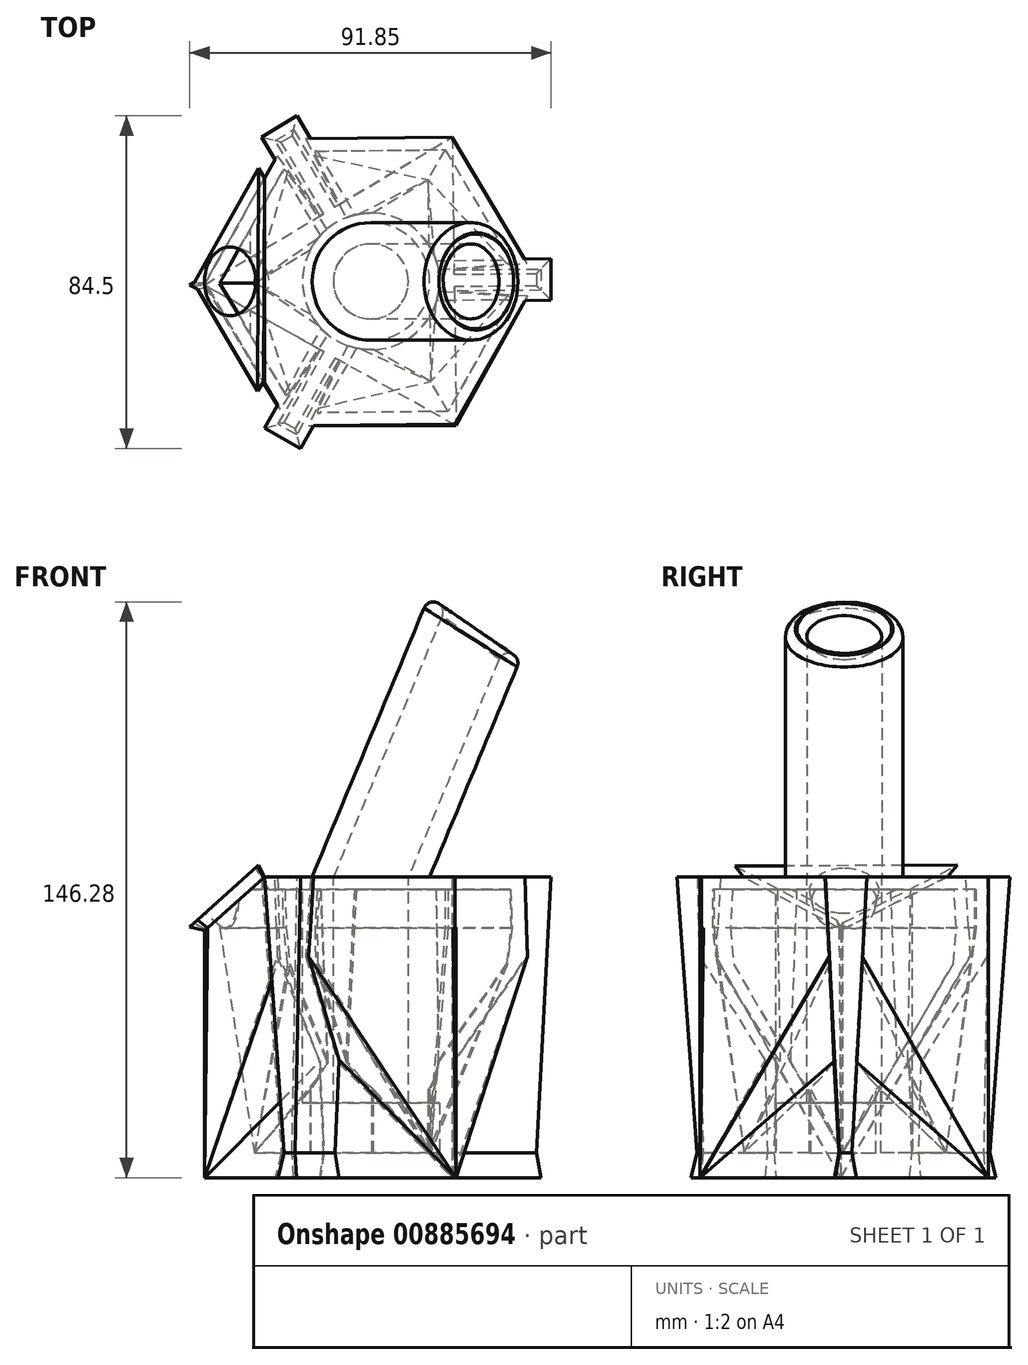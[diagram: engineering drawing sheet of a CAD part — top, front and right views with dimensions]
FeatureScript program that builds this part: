
annotation { "Feature Type Name" : "Feature", "Feature Type Description" : "" }
export const myFeature = defineFeature(function(context is Context, id is Id, definition is map)
    precondition{}
    {
        {
            var Q0;
            Q0=qCreatedBy(makeId("Top.planeOp"),FACE);
            var sketch = newSketch(context, id + "F0", { "sketchPlane" : qUnion([Q0])});
            skCircle(sketch, "E0.cCircle", {"center": v(0, -0.3) * mm, "radius": 21.17 * mm, "construction": true});
            skLineSegment(sketch, "E0.0", {"start": v(20.65, 36.66) * mm, "end": v(21.68, -36.66) * mm});
            skLineSegment(sketch, "E0.1", {"start": v(21.68, -36.66) * mm, "end": v(-42.33, -0.88) * mm});
            skLineSegment(sketch, "E0.2", {"start": v(-42.33, -0.88) * mm, "end": v(20.65, 36.66) * mm});
            skPoint(sketch, "E0.0.midPoint", {"position": v(21.16, 0) * mm});
            skSolve(sketch);
        }
        {
            var Q0;
            Q0=qCreatedBy(makeId("Top.planeOp"),FACE);
            cPlane(context, id + "F1", {"entities" : qUnion([Q0]), "cplaneType" : CPlaneType.OFFSET, "offset" : 63.5 * mm, "width" : 152.4 * mm, "height" : 152.4 * mm});
        }
        {
            var Q0;
            Q0=qCreatedBy(id+"F1.planeOp",FACE);
            var sketch = newSketch(context, id + "F2", { "sketchPlane" : qUnion([Q0])});
            skCircle(sketch, "E1.cCircle", {"center": v(0, 0) * mm, "radius": 36.44 * mm, "construction": true});
            skLineSegment(sketch, "E1.0", {"start": v(42.07, 0.44) * mm, "end": v(21.42, -36.22) * mm});
            skLineSegment(sketch, "E1.1", {"start": v(21.42, -36.22) * mm, "end": v(-20.65, -36.66) * mm});
            skLineSegment(sketch, "E1.2", {"start": v(-20.65, -36.66) * mm, "end": v(-42.07, -0.44) * mm});
            skLineSegment(sketch, "E1.3", {"start": v(-42.07, -0.44) * mm, "end": v(-21.42, 36.22) * mm});
            skLineSegment(sketch, "E1.4", {"start": v(-21.42, 36.22) * mm, "end": v(20.65, 36.66) * mm});
            skLineSegment(sketch, "E1.5", {"start": v(20.65, 36.66) * mm, "end": v(42.07, 0.44) * mm});
            skPoint(sketch, "E1.0.midPoint", {"position": v(31.75, -17.89) * mm});
            skSolve(sketch);
        }
        {
            var Q0;
            Q0=qCreatedBy(makeId("Front.planeOp"),FACE);
            var sketch = newSketch(context, id + "F3", { "sketchPlane" : qUnion([Q0])});
            skLineSegment(sketch, "E2", {"start": v(-42.33, 0) * mm, "end": v(-42.07, 63.5) * mm});
            skSolve(sketch);
        }
        {
            var Q0;
            Q0=sQuery(id+"F3.wireOp",EDGE,"E2");
            var Q1;
            Q1=sQuery(id+"F0.wireOp",VERTEX,"E0.2.start");
            var Q2;
            Q2=makeQuery(id+"F2.imprint","IMPRINT",FACE,{"disambiguationData":[TD([[makeQuery(id+"F2.imprint","IMPRINT",EDGE,{"derivedFrom":sQuery(id+"F2.wireOp",EDGE,"E1.0")}),-1.0]])]});
            var Q3;
            Q3=sQuery(id+"F3.wireOp",VERTEX,"E2.end");
            var Q4;
            Q4=sQuery(id+"F0.wireOp",VERTEX,"E0.2.start");
            loft(context, id + "F4", {"spine" : qUnion([Q0]), "sheetProfilesArray" : [{ "sheetProfileEntities" : qUnion([Q1]) }, { "sheetProfileEntities" : qUnion([Q2]) }], "connections" : [{ "connectionEntities" : qUnion([Q3, Q4]), "connectionEdgeQueries" : qUnion([]), "connectionEdgeParameters" : [] }]});
        }
        {
            var Q1;
            Q1=makeQuery(id+"F2.imprint","IMPRINT",FACE,{"disambiguationData":[TD([[makeQuery(id+"F2.imprint","IMPRINT",EDGE,{"derivedFrom":sQuery(id+"F2.wireOp",EDGE,"E1.0")}),-1.0]])]});
            var Q2;
            Q2=sQuery(id+"F0.wireOp",VERTEX,"E0.0.end");
            loft(context, id + "F5", {"operationType" : NewBodyOperationType.ADD, "sheetProfilesArray" : [{ "sheetProfileEntities" : qUnion([Q1]) }, { "sheetProfileEntities" : qUnion([Q2]) }]});
        }
        {
            var Q1;
            Q1=makeQuery(id+"F2.imprint","IMPRINT",FACE,{"disambiguationData":[TD([[makeQuery(id+"F2.imprint","IMPRINT",EDGE,{"derivedFrom":sQuery(id+"F2.wireOp",EDGE,"E1.0")}),-1.0]])]});
            var Q2;
            Q2=sQuery(id+"F0.wireOp",VERTEX,"E0.0.start");
            loft(context, id + "F6", {"operationType" : NewBodyOperationType.ADD, "sheetProfilesArray" : [{ "sheetProfileEntities" : qUnion([Q1]) }, { "sheetProfileEntities" : qUnion([Q2]) }]});
        }
        {
            var Q0;
            Q0=makeQuery(id+"F0.imprint","IMPRINT",FACE,{"disambiguationData":[TD([[makeQuery(id+"F0.imprint","IMPRINT",EDGE,{"derivedFrom":sQuery(id+"F0.wireOp",EDGE,"E0.0")}),-1.0]])]});
            var Q1;
            Q1=makeQuery(id+"F4.opLoft","CAP_FACE",FACE,{"disambiguationData":[OSD([makeQuery(id+"F2.imprint","IMPRINT",FACE,{"disambiguationData":[TD([[makeQuery(id+"F2.imprint","IMPRINT",EDGE,{"derivedFrom":sQuery(id+"F2.wireOp",EDGE,"E1.0")}),-1.0]])]})])],"isStart":true});
            extrude(context, id + "F7", {"entities" : qUnion([Q0]), "operationType" : NewBodyOperationType.ADD, "endBound" : BoundingType.UP_TO_SURFACE, "depth" : 66.55 * mm, "endBoundEntityFace" : qUnion([Q1]), "offsetDistance" : 25.4 * mm});
        }
        {
            var Q0;
            Q0=makeQuery(id+"F2.imprint","IMPRINT",FACE,{"disambiguationData":[TD([[makeQuery(id+"F2.imprint","IMPRINT",EDGE,{"derivedFrom":sQuery(id+"F2.wireOp",EDGE,"E1.0")}),-1.0]])]});
            extrude(context, id + "F8", {"entities" : qUnion([Q0]), "operationType" : NewBodyOperationType.ADD, "depth" : 7.87 * mm, "offsetDistance" : 25.4 * mm});
        }
        {
            var Q0;
            Q0=qCreatedBy(id+"F1.planeOp",FACE);
            var sketch = newSketch(context, id + "F9", { "sketchPlane" : qUnion([Q0])});
            skCircle(sketch, "E3.cCircle", {"center": v(0, 0) * mm, "radius": 38.41 * mm, "construction": true});
            skLineSegment(sketch, "E3.0", {"start": v(18.85, 33.46) * mm, "end": v(38.4, 0.4) * mm});
            skLineSegment(sketch, "E3.1", {"start": v(38.4, 0.4) * mm, "end": v(19.55, -33.06) * mm});
            skLineSegment(sketch, "E3.2", {"start": v(19.55, -33.06) * mm, "end": v(-18.85, -33.46) * mm});
            skLineSegment(sketch, "E3.3", {"start": v(-18.85, -33.46) * mm, "end": v(-38.4, -0.4) * mm});
            skLineSegment(sketch, "E3.4", {"start": v(-38.4, -0.4) * mm, "end": v(-19.55, 33.06) * mm});
            skLineSegment(sketch, "E3.5", {"start": v(-19.55, 33.06) * mm, "end": v(18.85, 33.46) * mm});
            skSolve(sketch);
        }
        {
            var Q0;
            Q0 = qSketchRegion(id + "F9", true);
            var Q1;
            Q1=sQuery(id+"F9.wireOp",EDGE,"54bb823f-575e-4e5f-845b-b7277e6f640d.0");
            var Q2;
            Q2=sQuery(id+"F9.wireOp",EDGE,"54bb823f-575e-4e5f-845b-b7277e6f640d.1");
            var Q3;
            Q3=sQuery(id+"F9.wireOp",EDGE,"54bb823f-575e-4e5f-845b-b7277e6f640d.2");
            extrude(context, id + "F10", {"entities" : qUnion([Q0]), "operationType" : NewBodyOperationType.REMOVE, "surfaceEntities" : qUnion([Q1, Q2, Q3]), "depth" : 36.83 * mm, "offsetDistance" : 25.4 * mm});
        }
        {
            var Q0;
            Q0=qCreatedBy(id+"F1.planeOp",FACE);
            var sketch = newSketch(context, id + "F11", { "sketchPlane" : qUnion([Q0])});
            skCircle(sketch, "E4.cCircle", {"center": v(0, 0) * mm, "radius": 38.41 * mm, "construction": true});
            skLineSegment(sketch, "E4.0", {"start": v(18.85, 33.46) * mm, "end": v(38.4, 0.4) * mm});
            skLineSegment(sketch, "E4.1", {"start": v(38.4, 0.4) * mm, "end": v(19.55, -33.06) * mm});
            skLineSegment(sketch, "E4.2", {"start": v(19.55, -33.06) * mm, "end": v(-18.85, -33.46) * mm});
            skLineSegment(sketch, "E4.3", {"start": v(-18.85, -33.46) * mm, "end": v(-38.4, -0.4) * mm});
            skLineSegment(sketch, "E4.4", {"start": v(-38.4, -0.4) * mm, "end": v(-19.55, 33.06) * mm});
            skLineSegment(sketch, "E4.5", {"start": v(-19.55, 33.06) * mm, "end": v(18.85, 33.46) * mm});
            skSolve(sketch);
        }
        {
            var Q0;
            Q0=qCreatedBy(makeId("Top.planeOp"),FACE);
            cPlane(context, id + "F12", {"entities" : qUnion([Q0]), "cplaneType" : CPlaneType.OFFSET, "offset" : 6.35 * mm, "width" : 152.4 * mm, "height" : 152.4 * mm});
        }
        {
            var Q0;
            Q0=qCreatedBy(id+"F12.planeOp",FACE);
            var sketch = newSketch(context, id + "F13", { "sketchPlane" : qUnion([Q0])});
            skCircle(sketch, "E5.cCircle", {"center": v(0, 0) * mm, "radius": 29.63 * mm, "construction": true});
            skLineSegment(sketch, "E5.0", {"start": v(14.45, 25.86) * mm, "end": v(15.17, -25.45) * mm});
            skLineSegment(sketch, "E5.1", {"start": v(15.17, -25.45) * mm, "end": v(-29.62, -0.41) * mm});
            skLineSegment(sketch, "E5.2", {"start": v(-29.62, -0.41) * mm, "end": v(14.45, 25.86) * mm});
            skSolve(sketch);
        }
        {
            var Q1;
            Q1=makeQuery(id+"F11.imprint","IMPRINT",FACE,{"disambiguationData":[TD([[makeQuery(id+"F11.imprint","IMPRINT",EDGE,{"derivedFrom":sQuery(id+"F11.wireOp",EDGE,"E4.0")}),-1.0]])]});
            var Q2;
            Q2=sQuery(id+"F13.wireOp",VERTEX,"E5.1.end");
            loft(context, id + "F14", {"operationType" : NewBodyOperationType.REMOVE, "sheetProfilesArray" : [{ "sheetProfileEntities" : qUnion([Q1]) }, { "sheetProfileEntities" : qUnion([Q2]) }]});
        }
        {
            var Q1;
            Q1=makeQuery(id+"F11.imprint","IMPRINT",FACE,{"disambiguationData":[TD([[makeQuery(id+"F11.imprint","IMPRINT",EDGE,{"derivedFrom":sQuery(id+"F11.wireOp",EDGE,"E4.0")}),-1.0]])]});
            var Q2;
            Q2=sQuery(id+"F13.wireOp",VERTEX,"E5.0.start");
            loft(context, id + "F15", {"operationType" : NewBodyOperationType.REMOVE, "sheetProfilesArray" : [{ "sheetProfileEntities" : qUnion([Q1]) }, { "sheetProfileEntities" : qUnion([Q2]) }]});
        }
        {
            var Q1;
            Q1=makeQuery(id+"F11.imprint","IMPRINT",FACE,{"disambiguationData":[TD([[makeQuery(id+"F11.imprint","IMPRINT",EDGE,{"derivedFrom":sQuery(id+"F11.wireOp",EDGE,"E4.0")}),-1.0]])]});
            var Q2;
            Q2=sQuery(id+"F13.wireOp",VERTEX,"E5.0.end");
            loft(context, id + "F16", {"operationType" : NewBodyOperationType.REMOVE, "sheetProfilesArray" : [{ "sheetProfileEntities" : qUnion([Q1]) }, { "sheetProfileEntities" : qUnion([Q2]) }]});
        }
        {
            var Q0;
            Q0 = qSketchRegion(id + "F13", true);
            extrude(context, id + "F17", {"entities" : qUnion([Q0]), "operationType" : NewBodyOperationType.REMOVE, "depth" : 76.2 * mm, "offsetDistance" : 25.4 * mm});
        }
        {
            var Q0;
            Q0=makeQuery(id+"F8.opExtrude","CAP_FACE",FACE,{"disambiguationData":[OSD([sQuery(id+"F2.wireOp",EDGE,"E1.0"),sQuery(id+"F2.wireOp",EDGE,"E1.1"),sQuery(id+"F2.wireOp",EDGE,"E1.2"),sQuery(id+"F2.wireOp",EDGE,"E1.3"),sQuery(id+"F2.wireOp",EDGE,"E1.4"),sQuery(id+"F2.wireOp",EDGE,"E1.5")])],"isStart":false});
            extrude(context, id + "F18", {"entities" : qUnion([Q0]), "operationType" : NewBodyOperationType.ADD, "depth" : 5.08 * mm, "offsetDistance" : 25.4 * mm});
        }
        {
            var Q0;
            Q0=qCreatedBy(id+"F12.planeOp",FACE);
            var sketch = newSketch(context, id + "F19", { "sketchPlane" : qUnion([Q0])});
            skLineSegment(sketch, "E6", {"start": v(-20.05, 37.02) * mm, "end": v(-22.79, 35.4) * mm});
            skLineSegment(sketch, "E7", {"start": v(-22.79, 35.4) * mm, "end": v(-1.83, 0) * mm});
            skLineSegment(sketch, "E8", {"start": v(-20.05, 37.02) * mm, "end": v(0.92, 1.59) * mm});
            skLineSegment(sketch, "E9", {"start": v(-1.83, 0) * mm, "end": v(-22.04, -35.88) * mm});
            skLineSegment(sketch, "E10", {"start": v(-22.04, -35.88) * mm, "end": v(-19.27, -37.44) * mm});
            skLineSegment(sketch, "E11", {"start": v(-19.27, -37.44) * mm, "end": v(0.92, -1.59) * mm});
            skLineSegment(sketch, "E12", {"start": v(0.92, -1.59) * mm, "end": v(42.1, -1.15) * mm});
            skLineSegment(sketch, "E13", {"start": v(42.1, -1.15) * mm, "end": v(42.06, 2.03) * mm});
            skLineSegment(sketch, "E14", {"start": v(42.06, 2.03) * mm, "end": v(0.92, 1.59) * mm});
            skSolve(sketch);
        }
        {
            var Q0;
            Q0 = qSketchRegion(id + "F19", true);
            var Q1;
            Q1=makeQuery(id+"F18.opExtrude","CAP_FACE",FACE,{"disambiguationData":[OSD([sQuery(id+"F2.wireOp",EDGE,"E1.0"),sQuery(id+"F2.wireOp",EDGE,"E1.1"),sQuery(id+"F2.wireOp",EDGE,"E1.2"),sQuery(id+"F2.wireOp",EDGE,"E1.3"),sQuery(id+"F2.wireOp",EDGE,"E1.4"),sQuery(id+"F2.wireOp",EDGE,"E1.5")])],"isStart":false});
            var Q2;
            Q2=makeQuery(id+"F7.opExtrude","CAP_FACE",FACE,{"disambiguationData":[OSD([sQuery(id+"F0.wireOp",EDGE,"E0.0"),sQuery(id+"F0.wireOp",EDGE,"E0.1"),sQuery(id+"F0.wireOp",EDGE,"E0.2")])],"isStart":true});
            extrude(context, id + "F20", {"entities" : qUnion([Q0]), "operationType" : NewBodyOperationType.ADD, "endBound" : BoundingType.UP_TO_SURFACE, "depth" : 25.4 * mm, "endBoundEntityFace" : qUnion([Q1]), "offsetDistance" : 25.4 * mm, "hasDraft" : true, "draftAngle" : 3 * degree, "hasSecondDirection" : true, "secondDirectionBound" : SecondDirectionBoundingType.UP_TO_SURFACE, "secondDirectionOppositeDirection" : true, "secondDirectionDepth" : 25.4 * mm, "secondDirectionBoundEntityFace" : qUnion([Q2]), "hasSecondDirectionDraft" : true, "secondDirectionDraftAngle" : 10 * degree});
        }
        {
            var Q0;
            Q0=makeQuery(id+"F20.boolean.opBoolean","MERGE",FACE,{"derivedFrom":[makeQuery(id+"F18.opExtrude","CAP_FACE",FACE,{"disambiguationData":[OSD([sQuery(id+"F2.wireOp",EDGE,"E1.0"),sQuery(id+"F2.wireOp",EDGE,"E1.1"),sQuery(id+"F2.wireOp",EDGE,"E1.2"),sQuery(id+"F2.wireOp",EDGE,"E1.3"),sQuery(id+"F2.wireOp",EDGE,"E1.4"),sQuery(id+"F2.wireOp",EDGE,"E1.5")])],"isStart":false}),makeQuery(id+"F20.opExtrude","CAP_FACE",FACE,{"disambiguationData":[OSD([sQuery(id+"F19.wireOp",EDGE,"E6"),sQuery(id+"F19.wireOp",EDGE,"E7"),sQuery(id+"F19.wireOp",EDGE,"E8"),sQuery(id+"F19.wireOp",EDGE,"E9"),sQuery(id+"F19.wireOp",EDGE,"E10"),sQuery(id+"F19.wireOp",EDGE,"E11"),sQuery(id+"F19.wireOp",EDGE,"E12"),sQuery(id+"F19.wireOp",EDGE,"E13"),sQuery(id+"F19.wireOp",EDGE,"E14")])],"isStart":false})]});
            var sketch = newSketch(context, id + "F21", { "sketchPlane" : qUnion([Q0])});
            skCircle(sketch, "E15", {"center": v(0, 0) * mm, "radius": 9.53 * mm});
            skCircle(sketch, "E16", {"center": v(0, 0) * mm, "radius": 17.37 * mm});
            skSolve(sketch);
        }
        {
            var Q0;
            Q0 = qSketchRegion(id + "F21", true);
            var Q1;
            Q1=makeQuery(id+"F20.boolean.opBoolean","MERGE",FACE,{"derivedFrom":[makeQuery(id+"F7.opExtrude","CAP_FACE",FACE,{"disambiguationData":[OSD([sQuery(id+"F0.wireOp",EDGE,"E0.0"),sQuery(id+"F0.wireOp",EDGE,"E0.1"),sQuery(id+"F0.wireOp",EDGE,"E0.2")])],"isStart":true}),makeQuery(id+"F20.opExtrude","CAP_FACE",FACE,{"disambiguationData":[OSD([sQuery(id+"F19.wireOp",EDGE,"E6"),sQuery(id+"F19.wireOp",EDGE,"E7"),sQuery(id+"F19.wireOp",EDGE,"E8"),sQuery(id+"F19.wireOp",EDGE,"E9"),sQuery(id+"F19.wireOp",EDGE,"E10"),sQuery(id+"F19.wireOp",EDGE,"E11"),sQuery(id+"F19.wireOp",EDGE,"E12"),sQuery(id+"F19.wireOp",EDGE,"E13"),sQuery(id+"F19.wireOp",EDGE,"E14")])],"isStart":true})]});
            extrude(context, id + "F22", {"entities" : qUnion([Q0]), "operationType" : NewBodyOperationType.ADD, "endBound" : BoundingType.UP_TO_SURFACE, "oppositeDirection" : true, "depth" : 70.61 * mm, "endBoundEntityFace" : qUnion([Q1]), "offsetDistance" : 25.4 * mm});
        }
        {
            var Q0;
            {var subQ0=sQuery(id+"F21.wireOp",EDGE,"E15");var subQ12=sQuery(id+"F19.wireOp",EDGE,"E8");var subQ37=sQuery(id+"F9.wireOp",EDGE,"E3.5");var subQ38=makeQuery(id+"F20.boolean.opBoolean","SPLIT",EDGE,{"disambiguationData":[TD([makeQuery(id+"F10.boolean.opBoolean","COPY",FACE,{"derivedFrom":makeQuery(id+"F10.opExtrude","SWEPT_FACE",FACE,{"disambiguationData":[OSD([subQ37])]})})])],"derivedFrom":makeQuery(id+"F20.opExtrude","CAP_EDGE",EDGE,{"disambiguationData":[OSD([subQ12])],"isStart":false})});var subQ40=makeQuery(id+"F21.imprint","INTERSECT",VERTEX,{"derivedFrom":[subQ38,subQ0]});Q0=makeQuery(id+"F21.imprint","IMPRINT",FACE,{"disambiguationData":[TD([[makeQuery(id+"F21.imprint","IMPRINT",EDGE,{"disambiguationData":[TD([[subQ40,-1.0]])],"derivedFrom":subQ0}),1.0]])]});}
            var Q1;
            Q1=makeQuery(id+"F20.*.split.splitOp","SPLIT",FACE,{"derivedFrom":makeQuery(id+"F20.opExtrude","SWEPT_FACE",FACE,{"disambiguationData":[OSD([sQuery(id+"F19.wireOp",EDGE,"E14")])]}),"isFromBackBody":true});
            extrude(context, id + "F23", {"entities" : qUnion([Q0]), "operationType" : NewBodyOperationType.REMOVE, "oppositeDirection" : true, "depth" : 69.85 * mm, "endBoundEntityFace" : qUnion([Q1]), "offsetDistance" : 25.4 * mm});
        }
        {
            var Q0;
            Q0=qCreatedBy(id+"F12.planeOp",FACE);
            var sketch = newSketch(context, id + "F24", { "sketchPlane" : qUnion([Q0])});
            skCircle(sketch, "E17", {"center": v(0, 0) * mm, "radius": 17.37 * mm});
            skSolve(sketch);
        }
        {
            var Q0;
            Q0 = qSketchRegion(id + "F24", true);
            extrude(context, id + "F25", {"entities" : qUnion([Q0]), "operationType" : NewBodyOperationType.REMOVE, "depth" : 12.7 * mm, "offsetDistance" : 25.4 * mm});
        }
        {
            var Q0;
            {var subQ8=sQuery(id+"F19.wireOp",EDGE,"E6");Q0=makeQuery(id+"F21.imprint","IMPRINT",FACE,{"disambiguationData":[TD([[makeQuery(id+"F21.imprint","IMPRINT",EDGE,{"derivedFrom":makeQuery(id+"F20.opExtrude","CAP_EDGE",EDGE,{"disambiguationData":[OSD([subQ8])],"isStart":false})}),1.0]])]});}
            var sketch = newSketch(context, id + "F26", { "sketchPlane" : qUnion([Q0])});
            skCircle(sketch, "E18.cCircle", {"center": v(0, 0) * mm, "radius": 42.08 * mm, "construction": true});
            skLineSegment(sketch, "E18.0", {"start": v(20.65, 36.66) * mm, "end": v(42.07, 0.44) * mm});
            skLineSegment(sketch, "E18.1", {"start": v(42.07, 0.44) * mm, "end": v(21.42, -36.22) * mm});
            skLineSegment(sketch, "E18.2", {"start": v(21.42, -36.22) * mm, "end": v(-20.65, -36.66) * mm});
            skLineSegment(sketch, "E18.3", {"start": v(-20.65, -36.66) * mm, "end": v(-42.07, -0.44) * mm});
            skLineSegment(sketch, "E18.4", {"start": v(-42.07, -0.44) * mm, "end": v(-21.42, 36.22) * mm});
            skLineSegment(sketch, "E18.5", {"start": v(-21.42, 36.22) * mm, "end": v(20.65, 36.66) * mm});
            skSolve(sketch);
        }
        {
            var Q0;
            Q0 = qSketchRegion(id + "F26", true);
            extrude(context, id + "F27", {"entities" : qUnion([Q0]), "operationType" : NewBodyOperationType.ADD, "oppositeDirection" : true, "depth" : 3.17 * mm, "offsetDistance" : 25.4 * mm});
        }
        {
            var Q0;
            {var subQ0=sQuery(id+"F21.wireOp",EDGE,"E15");var subQ8=sQuery(id+"F9.wireOp",EDGE,"E3.4");var subQ11=sQuery(id+"F19.wireOp",EDGE,"E7");var subQ14=makeQuery(id+"F20.boolean.opBoolean","SPLIT",EDGE,{"disambiguationData":[TD([makeQuery(id+"F10.boolean.opBoolean","COPY",FACE,{"derivedFrom":makeQuery(id+"F10.opExtrude","SWEPT_FACE",FACE,{"disambiguationData":[OSD([subQ8])]})})])],"derivedFrom":makeQuery(id+"F20.opExtrude","CAP_EDGE",EDGE,{"disambiguationData":[OSD([subQ11])],"isStart":false})});var subQ15=makeQuery(id+"F21.imprint","INTERSECT",VERTEX,{"derivedFrom":[subQ14,subQ0]});Q0=makeQuery(id+"F21.imprint","IMPRINT",FACE,{"disambiguationData":[TD([[makeQuery(id+"F21.imprint","IMPRINT",EDGE,{"disambiguationData":[TD([[subQ15,-1.0]])],"derivedFrom":subQ0}),1.0]])]});}
            var Q1;
            {var subQ0=sQuery(id+"F21.wireOp",EDGE,"E15");var subQ12=sQuery(id+"F19.wireOp",EDGE,"E8");var subQ37=sQuery(id+"F9.wireOp",EDGE,"E3.5");var subQ38=makeQuery(id+"F20.boolean.opBoolean","SPLIT",EDGE,{"disambiguationData":[TD([makeQuery(id+"F10.boolean.opBoolean","COPY",FACE,{"derivedFrom":makeQuery(id+"F10.opExtrude","SWEPT_FACE",FACE,{"disambiguationData":[OSD([subQ37])]})})])],"derivedFrom":makeQuery(id+"F20.opExtrude","CAP_EDGE",EDGE,{"disambiguationData":[OSD([subQ12])],"isStart":false})});var subQ40=makeQuery(id+"F21.imprint","INTERSECT",VERTEX,{"derivedFrom":[subQ38,subQ0]});Q1=makeQuery(id+"F21.imprint","IMPRINT",FACE,{"disambiguationData":[TD([[makeQuery(id+"F21.imprint","IMPRINT",EDGE,{"disambiguationData":[TD([[subQ40,-1.0]])],"derivedFrom":subQ0}),1.0]])]});}
            var Q2;
            {var subQ0=sQuery(id+"F21.wireOp",EDGE,"E15");var subQ2=sQuery(id+"F19.wireOp",EDGE,"E11");var subQ11=sQuery(id+"F9.wireOp",EDGE,"E3.2");var subQ14=makeQuery(id+"F20.boolean.opBoolean","SPLIT",EDGE,{"disambiguationData":[TD([makeQuery(id+"F10.boolean.opBoolean","COPY",FACE,{"derivedFrom":makeQuery(id+"F10.opExtrude","SWEPT_FACE",FACE,{"disambiguationData":[OSD([subQ11])]})})])],"derivedFrom":makeQuery(id+"F20.opExtrude","CAP_EDGE",EDGE,{"disambiguationData":[OSD([subQ2])],"isStart":false})});var subQ15=makeQuery(id+"F21.imprint","INTERSECT",VERTEX,{"derivedFrom":[subQ14,subQ0]});Q2=makeQuery(id+"F21.imprint","IMPRINT",FACE,{"disambiguationData":[TD([[makeQuery(id+"F21.imprint","IMPRINT",EDGE,{"disambiguationData":[TD([[subQ15,-1.0]])],"derivedFrom":subQ0}),1.0]])]});}
            var Q3;
            {var subQ0=sQuery(id+"F21.wireOp",EDGE,"E15");var subQ9=sQuery(id+"F19.wireOp",EDGE,"E8");var subQ11=sQuery(id+"F9.wireOp",EDGE,"E3.5");var subQ14=makeQuery(id+"F20.boolean.opBoolean","SPLIT",EDGE,{"disambiguationData":[TD([makeQuery(id+"F10.boolean.opBoolean","COPY",FACE,{"derivedFrom":makeQuery(id+"F10.opExtrude","SWEPT_FACE",FACE,{"disambiguationData":[OSD([subQ11])]})})])],"derivedFrom":makeQuery(id+"F20.opExtrude","CAP_EDGE",EDGE,{"disambiguationData":[OSD([subQ9])],"isStart":false})});var subQ15=makeQuery(id+"F21.imprint","INTERSECT",VERTEX,{"derivedFrom":[subQ14,subQ0]});Q3=makeQuery(id+"F21.imprint","IMPRINT",FACE,{"disambiguationData":[TD([[makeQuery(id+"F21.imprint","IMPRINT",EDGE,{"disambiguationData":[TD([[subQ15,1.0]])],"derivedFrom":subQ0}),1.0]])]});}
            var Q4;
            Q4=sQuery(id+"F21.wireOp",EDGE,"E15");
            extrude(context, id + "F28", {"entities" : qUnion([Q0, Q1, Q2, Q3]), "operationType" : NewBodyOperationType.REMOVE, "surfaceEntities" : qUnion([Q4]), "oppositeDirection" : true, "depth" : 6.35 * mm, "offsetDistance" : 25.4 * mm});
        }
        {
            var Q0;
            {var subQ8=sQuery(id+"F19.wireOp",EDGE,"E6");Q0=makeQuery(id+"F21.imprint","IMPRINT",FACE,{"disambiguationData":[TD([[makeQuery(id+"F21.imprint","IMPRINT",EDGE,{"derivedFrom":makeQuery(id+"F20.opExtrude","CAP_EDGE",EDGE,{"disambiguationData":[OSD([subQ8])],"isStart":false})}),1.0]])]});}
            var sketch = newSketch(context, id + "F29", { "sketchPlane" : qUnion([Q0])});
            skCircle(sketch, "E19", {"center": v(0, 0) * mm, "radius": 9.53 * mm});
            skCircle(sketch, "E20", {"center": v(0, 0) * mm, "radius": 12.7 * mm});
            skSolve(sketch);
        }
        {
            var Q0;
            {var subQ8=sQuery(id+"F19.wireOp",EDGE,"E6");Q0=makeQuery(id+"F29.imprint","IMPRINT",FACE,{"disambiguationData":[TD([[makeQuery(id+"F29.imprint","IMPRINT",EDGE,{"derivedFrom":makeQuery(id+"F21.imprint","IMPRINT",EDGE,{"derivedFrom":makeQuery(id+"F20.opExtrude","CAP_EDGE",EDGE,{"disambiguationData":[OSD([subQ8])],"isStart":false})})}),1.0]])]});}
            cPlane(context, id + "F30", {"entities" : qUnion([Q0]), "cplaneType" : CPlaneType.OFFSET, "offset" : 76.2 * mm, "width" : 152.4 * mm, "height" : 152.4 * mm});
        }
        {
            var Q0;
            Q0=qCreatedBy(id+"F30.planeOp",FACE);
            var sketch = newSketch(context, id + "F31", { "sketchPlane" : qUnion([Q0])});
            skCircle(sketch, "E21", {"center": v(31.75, 0) * mm, "radius": 9.53 * mm});
            skCircle(sketch, "E22", {"center": v(31.75, 0) * mm, "radius": 14.93 * mm});
            skSolve(sketch);
        }
        {
            var Q0;
            Q0=qCreatedBy(makeId("Front.planeOp"),FACE);
            var sketch = newSketch(context, id + "F32", { "sketchPlane" : qUnion([Q0])});
            skLineSegment(sketch, "E23", {"start": v(31.75, 152.65) * mm, "end": v(0, 76.45) * mm});
            skSolve(sketch);
        }
        {
            var Q0;
            Q0=makeQuery(id+"F29.imprint","IMPRINT",FACE,{"disambiguationData":[TD([[makeQuery(id+"F29.imprint","IMPRINT",EDGE,{"derivedFrom":sQuery(id+"F29.wireOp",EDGE,"E19")}),-1.0]])]});
            var Q1;
            Q1=makeQuery(id+"F31.imprint","IMPRINT",FACE,{"disambiguationData":[TD([[makeQuery(id+"F31.imprint","IMPRINT",EDGE,{"derivedFrom":sQuery(id+"F31.wireOp",EDGE,"E21")}),-1.0]])]});
            var Q2;
            Q2=sQuery(id+"F32.wireOp",EDGE,"E23");
            sweep(context, id + "F33", {"operationType" : NewBodyOperationType.ADD, "profiles" : qUnion([Q0, Q1]), "path" : qUnion([Q2])});
        }
        {
            var Q0;
            Q0=qCreatedBy(makeId("Front.planeOp"),FACE);
            var sketch = newSketch(context, id + "F34", { "sketchPlane" : qUnion([Q0])});
            skLineSegment(sketch, "E24", {"start": v(0, 157.7) * mm, "end": v(46.75, 125.63) * mm});
            skLineSegment(sketch, "E25", {"start": v(46.75, 125.63) * mm, "end": v(69.79, 143.24) * mm});
            skLineSegment(sketch, "E26", {"start": v(69.79, 143.24) * mm, "end": v(9.97, 177.78) * mm});
            skLineSegment(sketch, "E27", {"start": v(9.97, 177.78) * mm, "end": v(0, 157.7) * mm});
            skSolve(sketch);
        }
        {
            var Q0;
            Q0=makeQuery(id+"F34.imprint","IMPRINT",FACE,{"disambiguationData":[TD([[makeQuery(id+"F34.imprint","IMPRINT",EDGE,{"derivedFrom":sQuery(id+"F34.wireOp",EDGE,"E24")}),1.0]])]});
            var Q1;
            Q1 = qConstructionFilter(qBodyType(qCreatedBy(id + "F34" ,EDGE), BodyType.WIRE), ConstructionObject.NO);
            extrude(context, id + "F35", {"entities" : qUnion([Q0]), "operationType" : NewBodyOperationType.REMOVE, "surfaceEntities" : qUnion([Q1]), "endBound" : BoundingType.THROUGH_ALL, "oppositeDirection" : true, "depth" : 25.4 * mm, "offsetDistance" : 25.4 * mm, "hasSecondDirection" : true, "secondDirectionOppositeDirection" : false, "secondDirectionDepth" : 25.4 * mm});
        }
        {
            var Q0;
            Q0=makeQuery(id+"F35.boolean.opBoolean","INTERSECT",EDGE,{"derivedFrom":[makeQuery(id+"F33.opSweep","SWEPT_FACE",FACE,{"disambiguationData":[OSD([sQuery(id+"F29.wireOp",EDGE,"E19"),sQuery(id+"F32.wireOp",EDGE,"E23")])]}),makeQuery(id+"F35.opExtrude","SWEPT_FACE",FACE,{"disambiguationData":[OSD([sQuery(id+"F34.wireOp",EDGE,"E24")])]})]});
            var Q1;
            Q1=makeQuery(id+"F35.boolean.opBoolean","INTERSECT",EDGE,{"derivedFrom":[makeQuery(id+"F33.opSweep","SWEPT_FACE",FACE,{"disambiguationData":[OSD([sQuery(id+"F31.wireOp",EDGE,"E22"),sQuery(id+"F32.wireOp",EDGE,"E23")])]}),makeQuery(id+"F35.opExtrude","SWEPT_FACE",FACE,{"disambiguationData":[OSD([sQuery(id+"F34.wireOp",EDGE,"E24")])]})]});
            fillet(context, id + "F36", {"entities" : qUnion([Q0, Q1]), "radius" : 2.54 * mm, "tangentPropagation" : true, "allowEdgeOverflow" : false});
        }
        {
            var Q0;
            Q0=qCreatedBy(makeId("Front.planeOp"),FACE);
            var sketch = newSketch(context, id + "F37", { "sketchPlane" : qUnion([Q0])});
            skLineSegment(sketch, "E28", {"start": v(-48.75, 57.08) * mm, "end": v(-27.04, 76.45) * mm});
            skLineSegment(sketch, "E29", {"start": v(-27.04, 76.45) * mm, "end": v(-44.91, 87.8) * mm});
            skLineSegment(sketch, "E30", {"start": v(-44.91, 87.8) * mm, "end": v(-55.53, 62.05) * mm});
            skLineSegment(sketch, "E31", {"start": v(-55.53, 62.05) * mm, "end": v(-48.75, 57.08) * mm});
            skSolve(sketch);
        }
        {
            var Q0;
            Q0 = qSketchRegion(id + "F37", true);
            extrude(context, id + "F38", {"entities" : qUnion([Q0]), "operationType" : NewBodyOperationType.REMOVE, "oppositeDirection" : true, "depth" : 30.48 * mm, "offsetDistance" : 25.4 * mm, "hasSecondDirection" : true, "secondDirectionOppositeDirection" : false, "secondDirectionDepth" : 25.4 * mm});
        }
        {
            var Q0;
            Q0=makeQuery(id+"F38.boolean.opBoolean","COPY",FACE,{"derivedFrom":makeQuery(id+"F38.opExtrude","SWEPT_FACE",FACE,{"disambiguationData":[OSD([sQuery(id+"F37.wireOp",EDGE,"E28")])]})});
            var sketch = newSketch(context, id + "F39", { "sketchPlane" : qUnion([Q0])});
            skLineSegment(sketch, "E32", {"start": v(30.73, 26.24) * mm, "end": v(30.37, -25.4) * mm});
            skLineSegment(sketch, "E33", {"start": v(30.37, -25.4) * mm, "end": v(11.27, -1.32) * mm});
            skLineSegment(sketch, "E34", {"start": v(11.27, -1.32) * mm, "end": v(10.24, -0.88) * mm});
            skLineSegment(sketch, "E35", {"start": v(10.24, -0.88) * mm, "end": v(10.75, -0.66) * mm});
            skLineSegment(sketch, "E36", {"start": v(10.75, -0.66) * mm, "end": v(10.58, -0.45) * mm});
            skLineSegment(sketch, "E37", {"start": v(10.58, -0.45) * mm, "end": v(30.73, 26.24) * mm});
            skSolve(sketch);
        }
        {
            var Q0;
            Q0 = qSketchRegion(id + "F39", true);
            extrude(context, id + "F40", {"entities" : qUnion([Q0]), "operationType" : NewBodyOperationType.ADD, "depth" : 3.17 * mm, "offsetDistance" : 25.4 * mm, "hasDraft" : true, "draftAngle" : 15 * degree});
        }
        {
            var Q0;
            Q0=makeQuery(id+"F40.opExtrude","CAP_FACE",FACE,{"disambiguationData":[OSD([sQuery(id+"F39.wireOp",EDGE,"E32"),sQuery(id+"F39.wireOp",EDGE,"E33"),sQuery(id+"F39.wireOp",EDGE,"E34"),sQuery(id+"F39.wireOp",EDGE,"E35"),sQuery(id+"F39.wireOp",EDGE,"E36"),sQuery(id+"F39.wireOp",EDGE,"E37")])],"isStart":false});
            var sketch = newSketch(context, id + "F41", { "sketchPlane" : qUnion([Q0])});
            skCircle(sketch, "E38", {"center": v(21.84, 0) * mm, "radius": 8.73 * mm});
            skPoint(sketch, "E39", {"position": v(28.01, 0) * mm});
            skSolve(sketch);
        }
        {
            var Q0;
            Q0 = qSketchRegion(id + "F41", true);
            var Q1;
            Q1=sQuery(id+"F41.wireOp",EDGE,"E38");
            extrude(context, id + "F42", {"entities" : qUnion([Q0]), "operationType" : NewBodyOperationType.REMOVE, "surfaceEntities" : qUnion([Q1]), "oppositeDirection" : true, "depth" : 12.7 * mm, "offsetDistance" : 25.4 * mm, "hasDraft" : true, "draftAngle" : 10 * degree, "draftPullDirection" : true});
        }
    });
